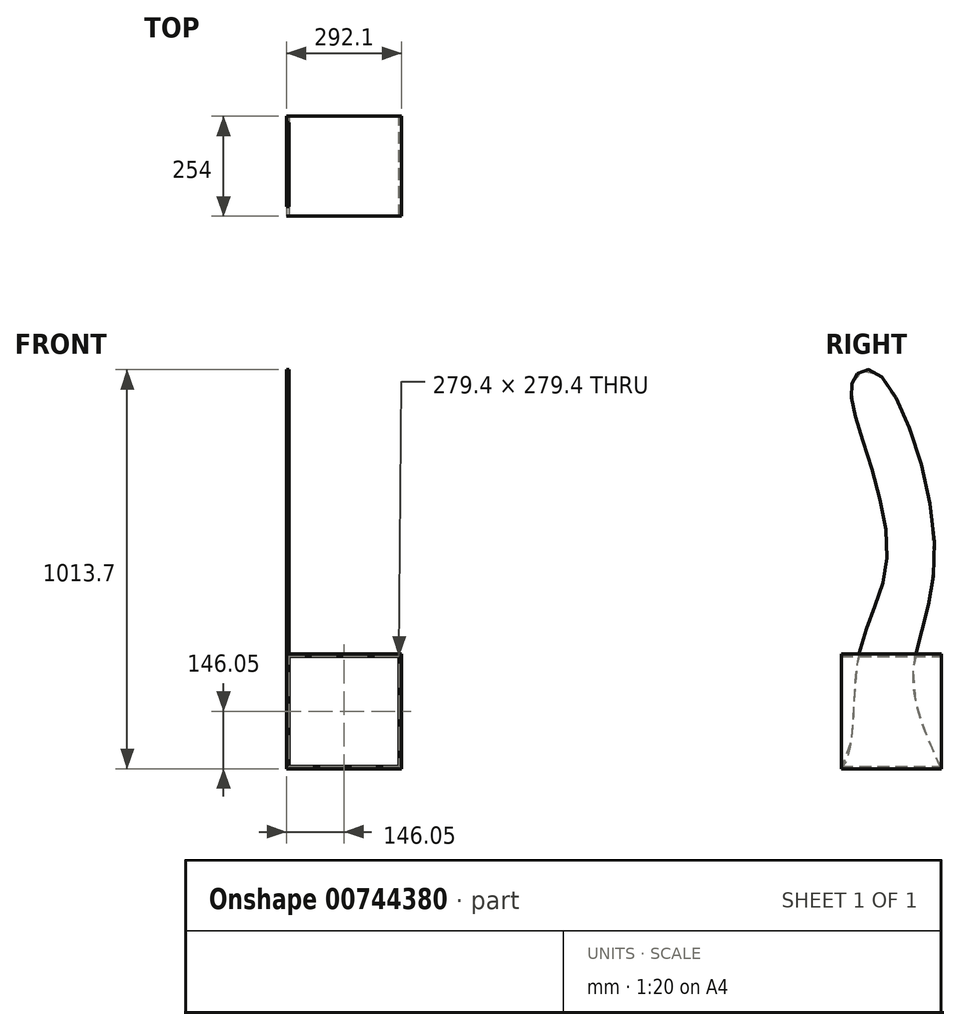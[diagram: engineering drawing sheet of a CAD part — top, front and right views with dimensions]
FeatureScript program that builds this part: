
annotation { "Feature Type Name" : "Feature", "Feature Type Description" : "" }
export const myFeature = defineFeature(function(context is Context, id is Id, definition is map)
    precondition{}
    {
        {
            var Q0;
            Q0=qCreatedBy(makeId("Front.planeOp"),FACE);
            var sketch = newSketch(context, id + "F0", { "sketchPlane" : qUnion([Q0])});
            skLineSegment(sketch, "E0.bottom", {"start": v(0, 0) * mm, "end": v(292.1, 0) * mm});
            skLineSegment(sketch, "E0.top", {"start": v(0, 292.1) * mm, "end": v(292.1, 292.1) * mm});
            skLineSegment(sketch, "E0.left", {"start": v(0, 0) * mm, "end": v(0, 292.1) * mm});
            skLineSegment(sketch, "E0.right", {"start": v(292.1, 0) * mm, "end": v(292.1, 292.1) * mm});
            skLineSegment(sketch, "E1.0", {"start": v(6.35, 6.35) * mm, "end": v(285.75, 6.35) * mm});
            skLineSegment(sketch, "E1.1", {"start": v(6.35, 6.35) * mm, "end": v(6.35, 285.75) * mm});
            skLineSegment(sketch, "E1.2", {"start": v(6.35, 285.75) * mm, "end": v(285.75, 285.75) * mm});
            skLineSegment(sketch, "E1.3", {"start": v(285.75, 6.35) * mm, "end": v(285.75, 285.75) * mm});
            skSolve(sketch);
        }
        {
            var Q0;
            Q0=makeQuery(id+"F0.imprint","IMPRINT",FACE,{"disambiguationData":[TD([[makeQuery(id+"F0.imprint","IMPRINT",EDGE,{"derivedFrom":sQuery(id+"F0.wireOp",EDGE,"E0.bottom")}),1.0]])]});
            extrude(context, id + "F1", {"entities" : qUnion([Q0]), "depth" : 254 * mm, "offsetDistance" : 25.4 * mm});
        }
        {
            var Q0;
            Q0=qCreatedBy(makeId("Right.planeOp"),FACE);
            var sketch = newSketch(context, id + "F2", { "sketchPlane" : qUnion([Q0])});
            skLineSegment(sketch, "E2.bottom", {"start": v(0, 0) * mm, "end": v(-254, 0) * mm});
            skLineSegment(sketch, "E2.top", {"start": v(-44.07, 1061.7) * mm, "end": v(-254, 1061.7) * mm, "construction": true});
            skLineSegment(sketch, "E2.left", {"start": v(-44.07, -5.1) * mm, "end": v(-44.07, 1061.7) * mm, "construction": true});
            skLineSegment(sketch, "E2.right", {"start": v(-254, 0) * mm, "end": v(-254, 1061.7) * mm, "construction": true});
            skPoint(sketch, "E3.3.internal.snap0", {"position": v(-165.08, 0) * mm});
            skPoint(sketch, "E3.6.internal.snap0", {"position": v(-137.35, 0) * mm});
            skFitSpline(sketch, "E3", {"points": [v(0, 0) * mm, v(-71.25, 238.26) * mm, v(-16.48, 546.34) * mm, v(-165.08, 1006.94) * mm, v(-219.58, 995.9) * mm, v(-219.58, 902.33) * mm, v(-137.35, 544.57) * mm, v(-211.78, 277.88) * mm, v(-254, 0) * mm, v(-349.65, -26.45) * mm], "startDerivative": vector(-926.63, 2035.05) * mm, "endDerivative": vector(-1094.87, -87.06) * mm});
            skSolve(sketch);
        }
        {
            var Q0;
            Q0 = qSketchRegion(id + "F2", true);
            extrude(context, id + "F3", {"entities" : qUnion([Q0]), "depth" : 6.35 * mm, "offsetDistance" : 25.4 * mm});
        }
    });
